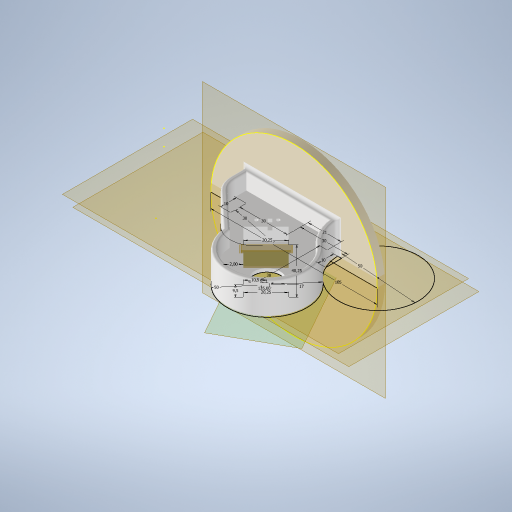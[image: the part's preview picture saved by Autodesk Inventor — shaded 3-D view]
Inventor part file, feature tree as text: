
AUTODESK INVENTOR PART (.ipt)
format: ipt  version: 2024 (Build 280153000, 153)  size: 1,030,656 bytes
history: native  units: mm
features: plane x9, extrude x8, other x8, fillet x7, projected_geometry x4, mirror x2, reference x2, sketch x1, chamfer x1
ambient origin geometry x8: Origin, YZ Plane, XZ Plane, XY Plane, X Axis, Y Axis, Z Axis, Center Point
bodies: Body1 (feature_tree)
feature tree (42):
  plane  "Work Plane1"
  extrude  "Extrusion2"  TaperAngle=0.0deg  [1 undecoded]
  plane  "Work Plane2"
  plane  "Work Plane4"
  sketch  "Sketch5"  dims[d2=5.0mm d3=0.0mm d9=0.0mm d10=105.0mm d11=90.0deg d12=5.0mm d13=30.0mm d14=30.0mm d16=21.0mm d17=38.0mm d26=10.5mm d27=135.0deg d28=9.5mm d30=20.25mm d31=40.25mm d32=20.25mm d33=10.0mm d34=10.0mm d35=30.0mm d36=0.349066mm d37=50.0mm d39=2.0mm d40=0.0mm d41=50.0mm d43=10.0mm d44=0.0mm d45=2.25mm d46=2.25mm d47=7.5mm d48=3.0mm d49=3.0mm d51=20.5mm d52=6.0mm d53=0.0mm d62=2.0mm d63=2.0mm d64=45.0deg d65=30.0mm d66=15.0mm d67=10.0mm d68=10.0mm d69=0.0mm d70=5.0mm d71=8.0mm d73=5.0mm d74=7.5mm d75=0.0mm d76=0.0mm d77=2.0mm d80=3.0mm d81=20.0mm d82=0.0mm d86=2.0mm d87=1.0mm d88=1.0mm d89=1.0mm d91=4.0mm d92=2.0mm d93=3.0mm d94=2.0mm d95=0.0mm d96=20.5mm d97=5.692388mm d111=1.0mm d112=1.0mm d113=6.146447mm d114=21.25mm d115=20.125mm d116=17.0mm d119=1.0mm d120=1.0mm d121=0.5mm d122=0.872665mm]
  extrude  "Extrusion3"  Depth=1.0mm
  extrude  "Extrusion4"  Depth=1.0mm TaperAngle=90.0deg
  plane  "Work Plane5"
  extrude  "Extrusion5"  Depth=1.0mm
  chamfer  "Chamfer2"  Distance=30.0mm
  extrude  "Extrusion7"  Depth=1.0mm
  extrude  "Extrusion8"  Depth=1.0mm
  fillet  "Fillet1"  Radius=10.5mm
  extrude  "Extrusion9"  TaperAngle=135.0deg  [1 undecoded]
  fillet  "Fillet2"  Radius=9.5mm
  fillet  "Fillet3"  Radius=20.25mm
  fillet  "Fillet4"  Radius=40.25mm
  fillet  "Fillet5"  Radius=20.25mm
  extrude  "Extrusion10"  Depth=10.0mm
  plane  "Work Plane6"
  plane  "Work Plane9"
  fillet  "Fillet12"  Radius=10.0mm
  fillet  "Fillet13"  Radius=30.0mm
  plane  "Work Plane10"
  mirror  "Mirror5"
  plane  "Work Plane11"
  mirror  "Mirror6"
  reference  "Reference4"
  reference  "Reference5"
  plane  "Work Plane3"
  projected_geometry  "Projected Loop2"
  projected_geometry  "Projected Loop4"
  projected_geometry  "Projected Loop5"
  projected_geometry  "Projected Loop7"
  other  "<userpath> windows\Documents\Inventor\Robotska_roka\Assembly4.iam"
  other  "Assembly4.iam"
  other  "Servo Motor MG996R  With Attachments:2"
  other  "attachmentCircular_1"
  other  "podloga:1"
  other  "<userpath> windows\Documents\Inventor\Robotska_roka\roka.iam"
  other  "roka.iam"
  other  "roka1:1"
note: 2 required parameter values undecoded (feature->parameter linkage not recoverable at this tier; creation-order binding heuristic only, values carry confidence <= 0.55)
